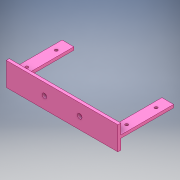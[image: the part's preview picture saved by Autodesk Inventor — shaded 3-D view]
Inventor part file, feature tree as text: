
AUTODESK INVENTOR PART (.ipt)
format: ipt  version: 2018 (Build 220112000, 112)  size: 142,336 bytes
history: native  units: mm
features: extrude x4, sketch x4
ambient origin geometry x8: Origin, YZ Plane, XZ Plane, XY Plane, X Axis, Y Axis, Z Axis, Center Point
bodies: Solid1 (feature_tree)
feature tree (8):
  extrude  "Extrusion1"  Depth=40.0mm
  extrude  "Extrusion2"  Depth=20.0mm
  extrude  "Extrusion3"  Depth=20.0mm
  extrude  "Extrusion4"  Depth=90.0mm TaperAngle=0.0deg
  sketch  "Sketch1"  dims[d0=190.0mm d1=40.0mm]
  sketch  "Sketch2"  dims[d2=5.0mm d3=0.0mm d4=20.0mm]
  sketch  "Sketch3"  dims[d5=5.0mm d6=20.0mm]
  sketch  "Sketch4"  dims[d7=5.0mm d8=90.0mm d9=0.0mm d10=8.0mm d11=8.0mm d12=60.0mm d14=90.0mm d15=0.0mm d17=5.0mm d18=5.0mm d19=5.0mm d20=5.0mm d21=50.0mm d22=50.0mm d23=20.0mm d24=20.0mm d25=90.0mm d26=0.0mm]
